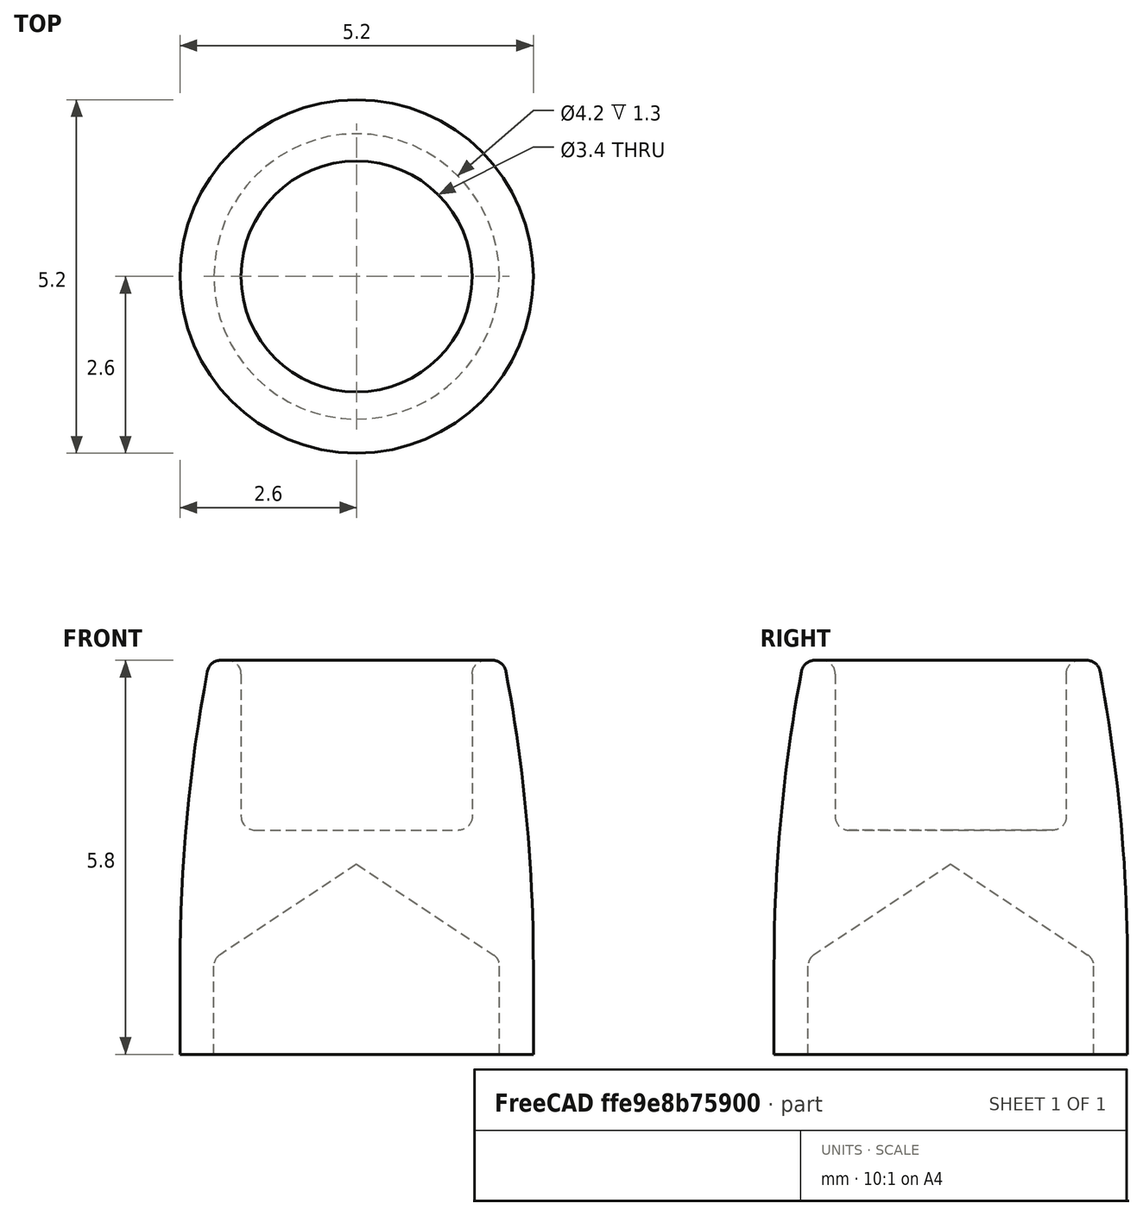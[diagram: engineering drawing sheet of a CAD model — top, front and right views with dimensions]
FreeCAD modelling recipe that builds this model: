
FCSTD DOCUMENT  (FreeCAD 0.18R16093 +53 (Git))
Label: MagnetHolderD3.4L4.5
License: All rights reserved
LicenseURL: http://en.wikipedia.org/wiki/All_rights_reserved
objects: Sketcher::SketchObject×1, PartDesign::Revolution×1, PartDesign::Body×1
note: 4 computed .brp shape members not serialized (recipe doc carries the construction recipe); baked Part::Feature solids carry a one-line shape summary decoded from their .brp

FEATURE [Sketcher::SketchObject] Sketch
  MapMode = 5
  Placement = pos=(0,0,0) rot=(1,0,0;1.5708rad)
  Support = -> [XZ_Plane]
  sketch-geometry (13):
    g0: LineSegment StartX=-2.6 StartY=0 StartZ=0 EndX=-2.6 EndY=-1.3 EndZ=0
    g1: LineSegment StartX=-2.6 StartY=-1.3 StartZ=0 EndX=-2.1 EndY=-1.3 EndZ=0
    g2: LineSegment StartX=-2.1 StartY=-1.3 StartZ=0 EndX=-2.1 EndY=0 EndZ=0
    g3: ArcOfCircle CenterX=20.9125 CenterY=0 CenterZ=0 NormalX=0 NormalY=0 NormalZ=1 AngleXU=0 Radius=23.5125 StartAngle=2.95608 EndAngle=3.14159
    g4: LineSegment StartX=-1.7 StartY=4.3 StartZ=0 EndX=-1.7 EndY=2.2 EndZ=0
    g5: LineSegment StartX=0 StartY=2 StartZ=0 EndX=0 EndY=1.5 EndZ=0
    g6: ArcOfCircle CenterX=-2 CenterY=4.3 CenterZ=0 NormalX=0 NormalY=0 NormalZ=1 AngleXU=0 Radius=0.2 StartAngle=1.5708 EndAngle=2.95608
    g7: LineSegment StartX=-2 StartY=4.5 StartZ=0 EndX=-1.9 EndY=4.5 EndZ=0
    g8: ArcOfCircle CenterX=-1.9 CenterY=4.3 CenterZ=0 NormalX=0 NormalY=0 NormalZ=1 AngleXU=0 Radius=0.2 StartAngle=0 EndAngle=1.5708
    g9: ArcOfCircle CenterX=-1.5 CenterY=2.2 CenterZ=0 NormalX=0 NormalY=0 NormalZ=1 AngleXU=0 Radius=0.2 StartAngle=3.14159 EndAngle=4.71239
    g10: LineSegment StartX=-1.5 StartY=2 StartZ=0 EndX=0 EndY=2 EndZ=0
    g11: LineSegment StartX=0 StartY=1.5 StartZ=0 EndX=-2.01054 EndY=0.166679 EndZ=0
    g12: ArcOfCircle CenterX=-1.9 CenterY=0 CenterZ=0 NormalX=0 NormalY=0 NormalZ=1 AngleXU=0 Radius=0.2 StartAngle=2.15637 EndAngle=3.14159
  constraints (35):
    c: Vertical(g0)
    c: Vertical(g2)
    c: Coincident(g1,g0)
    c: Coincident(g2,g1)
    c: Horizontal(g1)
    c: PointOnObject(g2,g-1)
    c: Tangent(g3,g0) = -1.5708
    c: DistanceX(g1,g1) = 0.5
    c: DistanceX(g2) = -2.1
    c: DistanceY(g2,g2) = 1.3
    c: PointOnObject(g5,g-2)
    c: Vertical(g4)
    c: Vertical(g5)
    c: Radius(g6) = 0.2
    c: Horizontal(g7)
    c: Tangent(g6,g7) = 1.5708
    c: Tangent(g8,g7) = 1.5708
    c: DistanceY(g7) = 4.5
    c: Tangent(g4,g8) = 1.5708
    c: DistanceX(g4) = -1.7
    c: Equal(g6,g8)
    c: Horizontal(g10)
    c: Tangent(g9,g4) = -1.5708
    c: Tangent(g9,g10) = -1.5708
    c: Coincident(g10,g5)
    c: Equal(g8,g9)
    c: DistanceY(g5,g5) = 0.5
    c: DistanceY(g9,g7) = 2.5
    c: Tangent(g3,g6) = -1.5708
    c: DistanceX(g7,g7) = 0.1
    c: PointOnObject(g0,g-1)
    c: Coincident(g11,g5)
    c: Tangent(g12,g11) = -1.5708
    c: Tangent(g12,g2) = 1.5708
    c: Equal(g12,g9)
FEATURE [PartDesign::Revolution] Revolution
  Angle = 360
  Axis = (0,2e-16,1)
  Base = (0,0,0)
  Placement = pos=(0,0,0) rot=(1,0,0;1.5708rad)
  Profile = -> Sketch
  ReferenceAxis = -> Sketch [V_Axis]
FEATURE [PartDesign::Body] Body
  Group = -> [Sketch,Revolution]
  Origin = -> Origin
  Tip = -> Revolution
